# Revit family: HARMANN - MOVO_EX
name_source: partatom
category: Mechanical Equipment
units: mm (PartAtom-declared; Revit-internal decimal feet)

## family parameters
Always vertical = Yes
Cut with Voids When Loaded = No
Maintain Annotation Orientation = No
OmniClass Number = 23.75.00.00
OmniClass Title = Climate Control (HVAC)
Part Type = Normal
Room Calculation Point = No
Round Connector Dimension = Use Diameter
Shared = No
Work Plane-Based = No

## types (12) — shared parameters
Autor = https://www.archispace.com
Description = Dachowy wentylator z wyrzutem poziomym
Lookup Table Name = MOVO
Manufacturer = Harmann Polska Sp. z o.o.
Opc Brak podstawy = Podstawa : Brak podstawy
Opc Podstawa Dachowa PR = Podstawa : Podstawa PR
Podstawa A = Podstawa : Brak podstawy
Podstawa B = Podstawa : Podstawa PR
Temperatura pracy ciągłej maksymalna T = 40 °C
Zasilanie Częstotliwość Maksymalna fmax = 50 Hz
Zasilanie Częstotliwość Minimalna fmin = 30 Hz
Zasilanie Częstotliwość Nominalna fnom = 50 Hz
Zasilanie Ilość faz = 3
Zasilanie napięcie nominalne Unom = 400 V
zero-valued in all types: Default Elevation

## per-type parameters (varying)
| type | Akc D | Akc EP | Akc PR | Akc SL | Ciśnienie akustyczne nominalne obudowa Lpa | DN | Klasa ATEX | MOVO S | Masa | Masa mmax | Moc akustyczna nominalna obudowa Lwa | N1 | Numer artykułu | Obroty nominalne nnom | Powietrze Przepływ Maksymalny Qmax | Powietrze ciśnienie statyczne maksymalne dPmax | Zasilanie Moc maksymalna Pmax | Zasilanie natężenie maksymalne Imax |
| MOVO.S 4-450/6100T EX | HARMANN - Akcesoria - D : D 400s | HARMANN - Akcesoria - EP : EP 400 | HARMANN - Akcesoria - PR : PR 450/400 | HARMANN - Akcesoria - SL : SL 400 | 55 dB(A) | 400 mm  [stored 1.31234 ft] | Ex II 2G c IIB T4 | HARMANN - Akcesoria - MOVO_S EX : MOVO.S 4-450/6100T EX | 56.00 kg | 86.00 kg | 84 dB(A) | 1 mm | 78251993 | 1410.000 RPM | 6100.00 m³/h | 590.0 Pa | 1100 W | 3 A |
| MOVO.S 6-450/4000T EX | HARMANN - Akcesoria - D : D 400s | HARMANN - Akcesoria - EP : EP 400 | HARMANN - Akcesoria - PR : PR 450/400 | HARMANN - Akcesoria - SL : SL 400 | 56 dB(A) | 400 mm  [stored 1.31234 ft] | Ex II 2G c IIB T5 | HARMANN - Akcesoria - MOVO_S EX : MOVO.S 6-450/4000T EX | 56.00 kg | 86.00 kg | 75 dB(A) | 2 mm | 78251994 | 920.000 RPM | 4000.00 m³/h | 260.0 Pa | 370 W | 1 A |
| MOVO.S 4-500/8000T EX | HARMANN - Akcesoria - D : D 450s | HARMANN - Akcesoria - EP : EP 450 | HARMANN - Akcesoria - PR : PR 500/450 | HARMANN - Akcesoria - SL : SL 450 | 68 dB(A) | 450 mm  [stored 1.47638 ft] | Ex II 2G c IIB T6 | HARMANN - Akcesoria - MOVO_S EX : MOVO.S 4-500/8000T EX | 75.00 kg | 115.00 kg | 87 dB(A) | 3 mm | 78251995 | 1410.000 RPM | 8000.00 m³/h | 730.0 Pa | 1600 W | 4 A |
| MOVO.S 6-500/5400T EX | HARMANN - Akcesoria - D : D 450s | HARMANN - Akcesoria - EP : EP 450 | HARMANN - Akcesoria - PR : PR 500/450 | HARMANN - Akcesoria - SL : SL 450 | 58 dB(A) | 450 mm  [stored 1.47638 ft] | Ex II 2G c IIB T7 | HARMANN - Akcesoria - MOVO_S EX : MOVO.S 6-500/5400T EX | 75.00 kg | 115.00 kg | 77 dB(A) | 4 mm | 78251996 | 915.000 RPM | 5400.00 m³/h | 330.0 Pa | 550 W | 2 A |
| MOVO.S 6-560/7900T EX | HARMANN - Akcesoria - D : D 500s | HARMANN - Akcesoria - EP : EP 500 | HARMANN - Akcesoria - PR : PR 560/500 | HARMANN - Akcesoria - SL : SL 560 | 62 dB(A) | 500 mm  [stored 1.64042 ft] | Ex II 2G c IIB T8 | HARMANN - Akcesoria - MOVO_S EX : MOVO.S 6-560/7900T EX | 100.00 kg | 140.00 kg | 81 dB(A) | 5 mm | 78251998 | 930.000 RPM | 7900.00 m³/h | 440.0 Pa | 1500 W | 4 A |
| MOVO.S 4-560/11900T EX | HARMANN - Akcesoria - D : D 500s | HARMANN - Akcesoria - EP : EP 500 | HARMANN - Akcesoria - PR : PR 560/500 | HARMANN - Akcesoria - SL : SL 500 | 71 dB(A) | 500 mm  [stored 1.64042 ft] | Ex II 2G c IIB T9 | HARMANN - Akcesoria - MOVO_S EX : MOVO.S 4-560/11900T EX | 100.00 kg | 140.00 kg | 90 dB(A) | 6 mm | 78251997 | 1400.000 RPM | 11900.00 m³/h | 980.0 Pa | 3200 W | 7 A |
| MOVO.S 4-630/17300T EX | HARMANN - Akcesoria - D : D 560s | HARMANN - Akcesoria - EP : EP 560 | HARMANN - Akcesoria - PR : PR 630/560 | HARMANN - Akcesoria - SL : SL 560 | 75 dB(A) | 560 mm  [stored 1.83727 ft] | Ex II 2G c IIB T10 | HARMANN - Akcesoria - MOVO_S EX : MOVO.S 4-630/17300T EX | 155.00 kg | 200.00 kg | 94 dB(A) | 7 mm | 78251999 | 1440.000 RPM | 17300.00 m³/h | 1210.0 Pa | 5500 W | 11 A |
| MOVO.S 6-630/11500T EX | HARMANN - Akcesoria - D : D 560s | HARMANN - Akcesoria - EP : EP 560 | HARMANN - Akcesoria - PR : PR 630/560 | HARMANN - Akcesoria - SL : SL 560 | 66 dB(A) | 560 mm  [stored 1.83727 ft] | Ex II 2G c IIB T11 | HARMANN - Akcesoria - MOVO_S EX : MOVO.S 6-630/11500T EX | 155.00 kg | 200.00 kg | 85 dB(A) | 8 mm | 78252000 | 940.000 RPM | 11500.00 m³/h | 540.0 Pa | 2200 W | 5 A |
| MOVO.S 4-710/20800T EX | HARMANN - Akcesoria - D : D 630s | HARMANN - Akcesoria - EP : EP 630 | HARMANN - Akcesoria - PR : PR 710/630 | HARMANN - Akcesoria - SL : SL 630 | 78 dB(A) | 630 mm  [stored 2.06693 ft] | Ex II 2G c IIB T12 | HARMANN - Akcesoria - MOVO_S EX : MOVO.S 4-710/20800T EX | 270.00 kg | 360.00 kg | 97 dB(A) | 9 mm | 78252001 | 1450.000 RPM | 20800.00 m³/h | 1340.0 Pa | 7500 W | 14 A |
| MOVO.S 6-710/14000T EX | HARMANN - Akcesoria - D : D 630s | HARMANN - Akcesoria - EP : EP 630 | HARMANN - Akcesoria - PR : PR 710/630 | HARMANN - Akcesoria - SL : SL 630 | 68 dB(A) | 630 mm  [stored 2.06693 ft] | Ex II 2G c IIB T13 | HARMANN - Akcesoria - MOVO_S EX : MOVO.S 6-710/14000T EX | 260.00 kg | 350.00 kg | 87 dB(A) | 10 mm | 78252002 | 980.000 RPM | 14000.00 m³/h | 610.0 Pa | 3000 W | 7 A |
| MOVO.S 4-800/35000T EX | HARMANN - Akcesoria - D : D 710s | HARMANN - Akcesoria - EP : EP 710 | HARMANN - Akcesoria - PR : PR 710/630 | HARMANN - Akcesoria - SL : SL 710 | 82 dB(A) | 710 mm  [stored 2.3294 ft] | Ex II 2G c IIB T14 | HARMANN - Akcesoria - MOVO_S EX : MOVO.S 4-800/35000T EX | 420.00 kg | 530.00 kg | 101 dB(A) | 11 mm | 78252003 | 1460.000 RPM | 35000.00 m³/h | 1890.0 Pa | 15000 W | 29 A |
| MOVO.S 6-800/22900T EX | HARMANN - Akcesoria - D : D 710s | HARMANN - Akcesoria - EP : EP 710 | HARMANN - Akcesoria - PR : PR 800/710 | HARMANN - Akcesoria - SL : SL 710 | 73 dB(A) | 710 mm  [stored 2.3294 ft] | Ex II 2G c IIB T13 | HARMANN - Akcesoria - MOVO_S EX : MOVO.S 6-800/22900T EX | 370.00 kg | 480.00 kg | 92 dB(A) | 12 mm | 78252004 | 960.000 RPM | 22900.00 m³/h | 810.0 Pa | 5500 W | 12 A |

note: column(s) folded — value = type name in every type: Model

note: [stored X ft] marks values corroborated as IEEE doubles in the binary element streams (Revit-internal decimal feet)

## geometry (parser evidence)
native form markers: Sweep x18
no freeform markers — native parametric forms only
